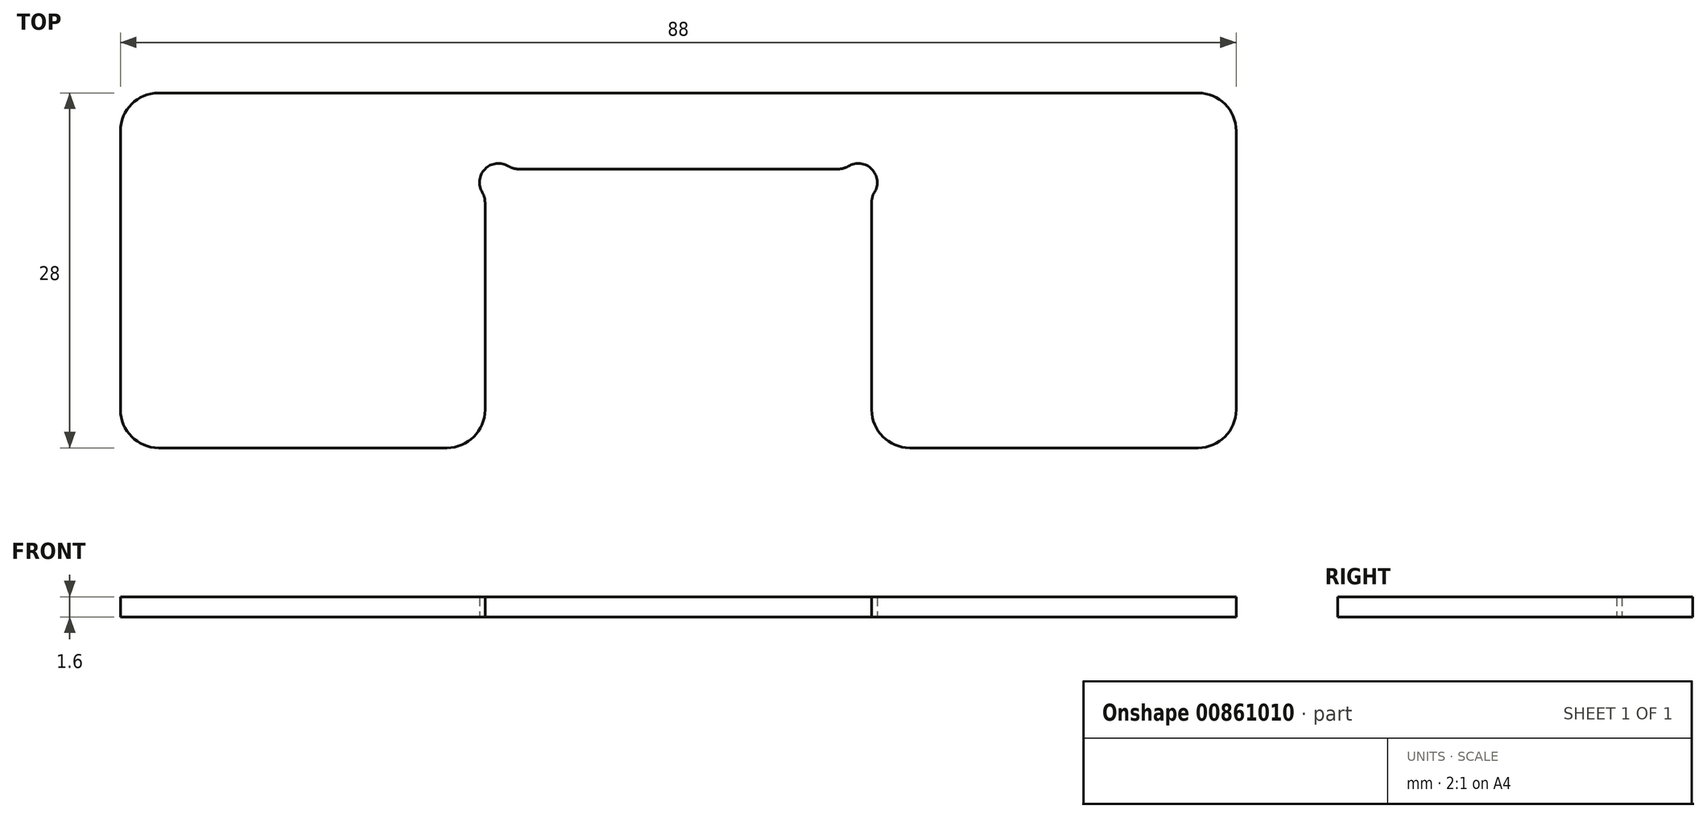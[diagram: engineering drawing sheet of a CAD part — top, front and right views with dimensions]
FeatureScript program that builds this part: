
annotation { "Feature Type Name" : "Feature", "Feature Type Description" : "" }
export const myFeature = defineFeature(function(context is Context, id is Id, definition is map)
    precondition{}
    {
        {
            var Q0;
            Q0=qCreatedBy(makeId("Top.planeOp"),FACE);
            var sketch = newSketch(context, id + "F0", { "sketchPlane" : qUnion([Q0])});
            skLineSegment(sketch, "E0.bottom", {"start": v(44, 14) * mm, "end": v(-44, 14) * mm});
            skLineSegment(sketch, "E0.top", {"start": v(44, -14) * mm, "end": v(15.25, -14) * mm});
            skLineSegment(sketch, "E0.left", {"start": v(44, 14) * mm, "end": v(44, -14) * mm});
            skLineSegment(sketch, "E0.right", {"start": v(-44, 14) * mm, "end": v(-44, -14) * mm});
            skPoint(sketch, "E0.middle", {"position": v(0, 0) * mm});
            skLineSegment(sketch, "E1", {"start": v(-15.25, -14) * mm, "end": v(-15.25, 8) * mm});
            skLineSegment(sketch, "E2", {"start": v(-15.25, 8) * mm, "end": v(15.25, 8) * mm});
            skLineSegment(sketch, "E3", {"start": v(15.25, 8) * mm, "end": v(15.25, -14) * mm});
            skLineSegment(sketch, "E4.trimOffspring", {"start": v(-15.25, -14) * mm, "end": v(-44, -14) * mm});
            skArc(sketch, "E5", {"start": v(-15.25, 5.38) * mm, "mid": v(-15.3, 5.78) * mm, "end": v(-15.47, 6.16) * mm});
            skArc(sketch, "E6", {"start": v(-13.4, 8.22) * mm, "mid": v(-15.25, 8) * mm, "end": v(-15.47, 6.16) * mm});
            skArc(sketch, "E7", {"start": v(-13.4, 8.22) * mm, "mid": v(-13.03, 8.06) * mm, "end": v(-12.63, 8) * mm});
            skArc(sketch, "E8.MirrorCS", {"start": v(13.4, 8.22) * mm, "mid": v(15.25, 8) * mm, "end": v(15.47, 6.16) * mm});
            skArc(sketch, "E9.MirrorCS", {"start": v(13.4, 8.22) * mm, "mid": v(13.03, 8.06) * mm, "end": v(12.63, 8) * mm});
            skArc(sketch, "E10.MirrorCS", {"start": v(15.25, 5.38) * mm, "mid": v(15.3, 5.78) * mm, "end": v(15.47, 6.16) * mm});
            skLineSegment(sketch, "E11", {"start": v(-15.25, 8) * mm, "end": v(-14.19, 6.94) * mm, "construction": true});
            skSolve(sketch);
        }
        {
            var Q0;
            Q0=makeQuery(id+"F0.imprint","IMPRINT",FACE,{"disambiguationData":[TD([[makeQuery(id+"F0.imprint","IMPRINT",EDGE,{"derivedFrom":sQuery(id+"F0.wireOp",EDGE,"E0.bottom")}),1.0]])]});
            extrude(context, id + "F1", {"entities" : qUnion([Q0]), "depth" : 1.6 * mm, "offsetDistance" : 25 * mm});
        }
        {
            var Q0;
            Q0=makeQuery(id+"F1.opExtrude","SWEPT_EDGE",EDGE,{"disambiguationData":[OSD([sQuery(id+"F0.wireOp",EDGE,"E1"),sQuery(id+"F0.wireOp",EDGE,"E4.trimOffspring")])]});
            var Q1;
            Q1=makeQuery(id+"F1.opExtrude","SWEPT_EDGE",EDGE,{"disambiguationData":[OSD([sQuery(id+"F0.wireOp",EDGE,"E0.right"),sQuery(id+"F0.wireOp",EDGE,"E4.trimOffspring")])]});
            var Q2;
            Q2=makeQuery(id+"F1.opExtrude","SWEPT_EDGE",EDGE,{"disambiguationData":[OSD([sQuery(id+"F0.wireOp",EDGE,"E0.bottom"),sQuery(id+"F0.wireOp",EDGE,"E0.right")])]});
            var Q3;
            Q3=makeQuery(id+"F1.opExtrude","SWEPT_EDGE",EDGE,{"disambiguationData":[OSD([sQuery(id+"F0.wireOp",EDGE,"E0.bottom"),sQuery(id+"F0.wireOp",EDGE,"E0.left")])]});
            var Q4;
            Q4=makeQuery(id+"F1.opExtrude","SWEPT_EDGE",EDGE,{"disambiguationData":[OSD([sQuery(id+"F0.wireOp",EDGE,"E0.top"),sQuery(id+"F0.wireOp",EDGE,"E0.left")])]});
            var Q5;
            Q5=makeQuery(id+"F1.opExtrude","SWEPT_EDGE",EDGE,{"disambiguationData":[OSD([sQuery(id+"F0.wireOp",EDGE,"E0.top"),sQuery(id+"F0.wireOp",EDGE,"E3")])]});
            fillet(context, id + "F2", {"entities" : qUnion([Q0, Q1, Q2, Q3, Q4, Q5]), "radius" : 3 * mm, "tangentPropagation" : true, "allowEdgeOverflow" : false});
        }
    });
